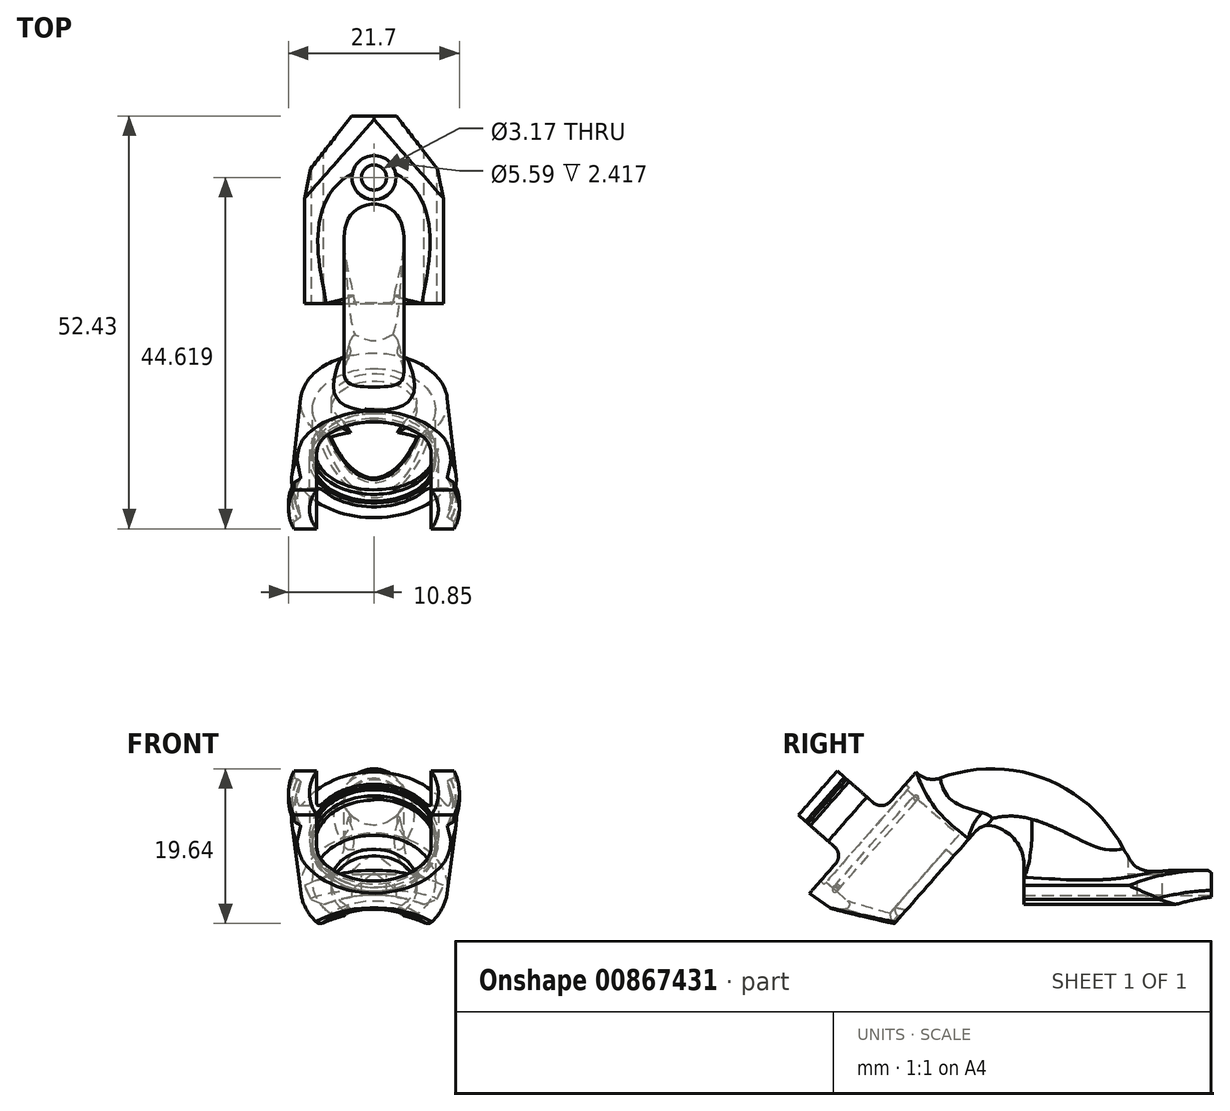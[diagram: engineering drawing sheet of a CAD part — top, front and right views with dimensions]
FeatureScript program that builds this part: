
annotation { "Feature Type Name" : "Feature", "Feature Type Description" : "" }
export const myFeature = defineFeature(function(context is Context, id is Id, definition is map)
    precondition{}
    {
        {
            var Q0;
            Q0=qCreatedBy(makeId("Front.planeOp"),FACE);
            var sketch = newSketch(context, id + "F0", { "sketchPlane" : qUnion([Q0])});
            skCircle(sketch, "E0", {"center": v(0, 0) * mm, "radius": 17.69 * mm, "construction": true});
            skCircle(sketch, "E1", {"center": v(0, 0) * mm, "radius": 14.13 * mm});
            skSolve(sketch);
        }
        {
            var Q0;
            Q0=qCreatedBy(makeId("Right.planeOp"),FACE);
            var sketch = newSketch(context, id + "F1", { "sketchPlane" : qUnion([Q0])});
            skLineSegment(sketch, "E2.0", {"start": v(0, -17.69) * mm, "end": v(0, 17.69) * mm, "construction": true});
            skLineSegment(sketch, "E3", {"start": v(0, 17.69) * mm, "end": v(-11.11, 17.69) * mm, "construction": true});
            skLineSegment(sketch, "E4", {"start": v(0, 17.69) * mm, "end": v(12.7, 17.69) * mm});
            skLineSegment(sketch, "E5", {"start": v(0, 17.69) * mm, "end": v(-11.11, 17.69) * mm});
            skLineSegment(sketch, "E6", {"start": v(-11.11, 17.69) * mm, "end": v(-11.11, 20.86) * mm});
            skLineSegment(sketch, "E7", {"start": v(-11.11, 20.86) * mm, "end": v(12.7, 20.86) * mm});
            skLineSegment(sketch, "E8", {"start": v(12.7, 20.86) * mm, "end": v(12.7, 17.69) * mm});
            skLineSegment(sketch, "E9", {"start": v(0, 0) * mm, "end": v(-2.54, 0) * mm, "construction": true});
            skLineSegment(sketch, "E10", {"start": v(-11.11, 17.69) * mm, "end": v(-22.65, 17.69) * mm, "construction": true});
            skLineSegment(sketch, "E11", {"start": v(-2.54, 0) * mm, "end": v(-22.65, 17.69) * mm});
            skLineSegment(sketch, "E12", {"start": v(-2.54, 0) * mm, "end": v(2.5, 5.72) * mm});
            skLineSegment(sketch, "E13", {"start": v(2.5, 5.72) * mm, "end": v(-11.11, 17.69) * mm});
            skLineSegment(sketch, "E14", {"start": v(-2.54, 0) * mm, "end": v(-7.57, -5.72) * mm});
            skLineSegment(sketch, "E15", {"start": v(-7.57, -5.72) * mm, "end": v(-34.2, 17.69) * mm});
            skLineSegment(sketch, "E16", {"start": v(-29.66, 13.58) * mm, "end": v(-24.51, 19.44) * mm, "construction": true});
            skLineSegment(sketch, "E17", {"start": v(-19.36, 25.3) * mm, "end": v(-25.92, 31.06) * mm});
            skLineSegment(sketch, "E18", {"start": v(-19.36, 25.3) * mm, "end": v(-20.93, 23.5) * mm});
            skLineSegment(sketch, "E19", {"start": v(-20.93, 23.5) * mm, "end": v(-19.98, 22.67) * mm});
            skLineSegment(sketch, "E20", {"start": v(-19.98, 22.67) * mm, "end": v(-17.4, 25.6) * mm});
            skLineSegment(sketch, "E21", {"start": v(-17.4, 25.6) * mm, "end": v(-24.91, 32.2) * mm});
            skLineSegment(sketch, "E22", {"start": v(-25.92, 31.06) * mm, "end": v(-24.91, 32.2) * mm});
            skLineSegment(sketch, "E23", {"start": v(-25.67, 31.35) * mm, "end": v(-31.87, 36.8) * mm});
            skLineSegment(sketch, "E24", {"start": v(-31.87, 36.8) * mm, "end": v(-31.11, 37.66) * mm});
            skLineSegment(sketch, "E25", {"start": v(-24.91, 32.2) * mm, "end": v(-31.11, 37.66) * mm});
            skLineSegment(sketch, "E26", {"start": v(-31.11, 37.66) * mm, "end": v(-30.1, 38.8) * mm});
            skLineSegment(sketch, "E27", {"start": v(-30.1, 38.8) * mm, "end": v(-28.91, 37.75) * mm});
            skLineSegment(sketch, "E28", {"start": v(-28.91, 37.75) * mm, "end": v(-29.92, 36.6) * mm});
            skLineSegment(sketch, "E29", {"start": v(-24.51, 19.44) * mm, "end": v(-29.7, 24) * mm, "construction": true});
            skCircle(sketch, "E30", {"center": v(-24.81, 30.09) * mm, "radius": 0.33 * mm});
            skLineSegment(sketch, "E31", {"start": v(-27.34, 34.34) * mm, "end": v(-26.59, 35.2) * mm});
            skLineSegment(sketch, "E32", {"start": v(-26.59, 35.2) * mm, "end": v(-17.4, 25.6) * mm});
            skLineSegment(sketch, "E33", {"start": v(-22.65, 17.69) * mm, "end": v(-34.2, 17.69) * mm, "construction": true});
            skPoint(sketch, "E34", {"position": v(-28.42, 17.69) * mm});
            skLineSegment(sketch, "E35", {"start": v(-24.51, 19.44) * mm, "end": v(-19.36, 25.3) * mm, "construction": true});
            skPoint(sketch, "E36", {"position": v(-27.09, 16.51) * mm});
            skLineSegment(sketch, "E37", {"start": v(-26.59, 35.2) * mm, "end": v(-29.5, 37.09) * mm});
            skSolve(sketch);
        }
        {
            var Q0;
            Q0=makeQuery(id+"F1.imprint","IMPRINT",FACE,{"disambiguationData":[TD([[makeQuery(id+"F1.imprint","IMPRINT",EDGE,{"derivedFrom":sQuery(id+"F1.wireOp",EDGE,"E4")}),1.0]])]});
            var Q1;
            Q1=sQuery(id+"F1.wireOp",EDGE,"E9");
            revolve(context, id + "F2", {"surfaceOperationType" : NewSurfaceOperationType.NEW, "entities" : qUnion([Q0]), "axis" : qUnion([Q1]), "revolveType" : RevolveType.SYMMETRIC, "angle" : 50 * degree});
        }
        {
            var Q0;
            {var subQ0=sQuery(id+"F1.wireOp",EDGE,"E17");Q0=makeQuery(id+"F1.imprint","IMPRINT",FACE,{"disambiguationData":[TD([[makeQuery(id+"F1.imprint","IMPRINT",EDGE,{"derivedFrom":subQ0}),-1.0]])]});}
            var Q1;
            {var subQ5=sQuery(id+"F1.wireOp",EDGE,"E23");Q1=makeQuery(id+"F1.imprint","IMPRINT",FACE,{"disambiguationData":[TD([[makeQuery(id+"F1.imprint","IMPRINT",EDGE,{"derivedFrom":subQ5}),-1.0]])]});}
            var Q2;
            {var subQ0=sQuery(id+"F1.wireOp",EDGE,"E26");Q2=makeQuery(id+"F1.imprint","IMPRINT",FACE,{"disambiguationData":[TD([[makeQuery(id+"F1.imprint","IMPRINT",EDGE,{"derivedFrom":subQ0}),-1.0]])]});}
            var Q3;
            {var subQ0=sQuery(id+"F1.wireOp",EDGE,"E21");Q3=makeQuery(id+"F1.imprint","IMPRINT",FACE,{"disambiguationData":[TD([[makeQuery(id+"F1.imprint","IMPRINT",EDGE,{"derivedFrom":subQ0}),-1.0]])]});}
            var Q4;
            {var subQ0=sQuery(id+"F1.wireOp",EDGE,"E30");var subQ1=sQuery(id+"F1.wireOp",EDGE,"E17");var subQ2=makeQuery(id+"F1.imprint","INTERSECT",VERTEX,{"disambiguationData":[OD(0.0)],"derivedFrom":[subQ1,subQ0]});Q4=makeQuery(id+"F1.imprint","IMPRINT",FACE,{"disambiguationData":[TD([[makeQuery(id+"F1.imprint","IMPRINT",EDGE,{"disambiguationData":[TD([[subQ2,-1.0]])],"derivedFrom":subQ1}),-1.0]])]});}
            var Q5;
            {var subQ5=sQuery(id+"F1.wireOp",EDGE,"1z6JYlKL-7tiU-9kOK-F6vj-neqsAa9XEWl2");Q5=makeQuery(id+"F1.imprint","IMPRINT",FACE,{"disambiguationData":[TD([[makeQuery(id+"F1.imprint","IMPRINT",EDGE,{"derivedFrom":subQ5}),1.0]])]});}
            var Q6;
            {var subQ3=sQuery(id+"F1.wireOp",EDGE,"E31");Q6=makeQuery(id+"F1.imprint","IMPRINT",FACE,{"disambiguationData":[TD([[makeQuery(id+"F1.imprint","IMPRINT",EDGE,{"derivedFrom":subQ3}),1.0]])]});}
            var Q7;
            Q7=sQuery(id+"F1.wireOp",EDGE,"E29");
            revolve(context, id + "F3", {"surfaceOperationType" : NewSurfaceOperationType.NEW, "entities" : qUnion([Q0, Q1, Q2, Q3, Q4, Q5, Q6]), "axis" : qUnion([Q7]), "revolveType" : RevolveType.FULL});
        }
        {
            var Q0;
            Q0=qCreatedBy(makeId("Top.planeOp"),FACE);
            cPlane(context, id + "F4", {"entities" : qUnion([Q0]), "cplaneType" : CPlaneType.OFFSET, "offset" : 20.32 * mm, "width" : 152.4 * mm, "height" : 152.4 * mm});
        }
        {
            var Q0;
            Q0=qCreatedBy(id+"F4.planeOp",FACE);
            var sketch = newSketch(context, id + "F5", { "sketchPlane" : qUnion([Q0])});
            skPoint(sketch, "E38.0", {"position": v(0, -11.11) * mm});
            skCircle(sketch, "E39", {"center": v(0, 4.89) * mm, "radius": 1.59 * mm});
            skSolve(sketch);
        }
        {
            var Q0;
            Q0=makeQuery(id+"F5.imprint","IMPRINT",FACE,{"disambiguationData":[TD([[makeQuery(id+"F5.imprint","IMPRINT",EDGE,{"derivedFrom":sQuery(id+"F5.wireOp",EDGE,"E39")}),1.0]])]});
            extrude(context, id + "F6", {"entities" : qUnion([Q0]), "operationType" : NewBodyOperationType.REMOVE, "endBound" : BoundingType.SYMMETRIC, "oppositeDirection" : true, "depth" : 25.4 * mm, "offsetDistance" : 25.4 * mm});
        }
        {
            var Q0;
            Q0=qCreatedBy(id+"F4.planeOp",FACE);
            var sketch = newSketch(context, id + "F7", { "sketchPlane" : qUnion([Q0])});
            skCircle(sketch, "E40", {"center": v(0, -0.95) * mm, "radius": 3.81 * mm});
            skPoint(sketch, "E41.0", {"position": v(0, -11.11) * mm});
            skSolve(sketch);
        }
        {
            var Q0;
            Q0=qCreatedBy(makeId("Right.planeOp"),FACE);
            var sketch = newSketch(context, id + "F8", { "sketchPlane" : qUnion([Q0])});
            skPoint(sketch, "E42.0", {"position": v(-11.11, 20.32) * mm});
            skLineSegment(sketch, "E42.1", {"start": v(3.3, 20.32) * mm, "end": v(6.48, 20.32) * mm, "construction": true});
            skLineSegment(sketch, "E43.0", {"start": v(-25.92, 31.06) * mm, "end": v(-36.22, 19.35) * mm, "construction": true});
            skLineSegment(sketch, "E43.1", {"start": v(-19.36, 25.3) * mm, "end": v(-29.66, 13.58) * mm, "construction": true});
            skLineSegment(sketch, "E44", {"start": v(-19.36, 25.3) * mm, "end": v(-25.92, 31.06) * mm, "construction": true});
            skArc(sketch, "E45", {"start": v(-0.95, 20.32) * mm, "mid": v(-10, 29.21) * mm, "end": v(-22.64, 28.18) * mm});
            skLineSegment(sketch, "E46.0", {"start": v(-4.76, 20.32) * mm, "end": v(2.86, 20.32) * mm});
            skPoint(sketch, "E47", {"position": v(-0.95, 20.32) * mm});
            skArc(sketch, "E48", {"start": v(-0.95, 20.32) * mm, "mid": v(-10.69, 29.44) * mm, "end": v(-23.88, 27.4) * mm});
            skLineSegment(sketch, "E49", {"start": v(-20.28, 24.25) * mm, "end": v(-26.84, 30.01) * mm});
            skSolve(sketch);
        }
        {
            var Q0;
            Q0 = qSketchRegion(id + "F7", true);
            var Q1;
            Q1=sQuery(id+"F8.wireOp",EDGE,"E48");
            sweep(context, id + "F9", {"operationType" : NewBodyOperationType.ADD, "profiles" : qUnion([Q0]), "path" : qUnion([Q1])});
        }
        {
            var Q0;
            Q0=makeQuery(id+"F2.opRevolve","CAP_EDGE",EDGE,{"disambiguationData":[OSD([sQuery(id+"F1.wireOp",EDGE,"E4"),sQuery(id+"F1.wireOp",EDGE,"E5")])],"isStart":true});
            var Q1;
            Q1=makeQuery(id+"F2.opRevolve","CAP_EDGE",EDGE,{"disambiguationData":[OSD([sQuery(id+"F1.wireOp",EDGE,"E4"),sQuery(id+"F1.wireOp",EDGE,"E5")])],"isStart":false});
            chamfer(context, id + "F10", {"entities" : qUnion([Q0, Q1]), "width" : 1.27 * mm, "tangentPropagation" : true});
        }
        {
            var Q0;
            Q0=makeQuery(id+"F0.imprint","IMPRINT",FACE,{"disambiguationData":[TD([[makeQuery(id+"F0.imprint","IMPRINT",EDGE,{"derivedFrom":sQuery(id+"F0.wireOp",EDGE,"E1")}),1.0]])]});
            extrude(context, id + "F11", {"entities" : qUnion([Q0]), "operationType" : NewBodyOperationType.REMOVE, "depth" : 43.43 * mm, "offsetDistance" : 25.4 * mm, "hasDraft" : true, "draftAngle" : 3 * degree});
        }
        {
            var Q0;
            Q0=qCreatedBy(id+"F4.planeOp",FACE);
            var sketch = newSketch(context, id + "F12", { "sketchPlane" : qUnion([Q0])});
            skCircle(sketch, "E50.0", {"center": v(0, 4.89) * mm, "radius": 1.59 * mm});
            skCircle(sketch, "E51", {"center": v(0, 4.89) * mm, "radius": 2.8 * mm});
            skSolve(sketch);
        }
        {
            var Q0;
            Q0=makeQuery(id+"F3.opRevolve","SWEPT_EDGE",EDGE,{"disambiguationData":[OSD([sQuery(id+"F1.wireOp",EDGE,"E25"),sQuery(id+"F1.wireOp",EDGE,"E28")])]});
            chamfer(context, id + "F13", {"entities" : qUnion([Q0]), "width" : 0.38 * mm, "tangentPropagation" : true});
        }
        {
            var Q0;
            Q0=makeQuery(id+"F3.opRevolve","SWEPT_FACE",FACE,{"disambiguationData":[OSD([sQuery(id+"F1.wireOp",EDGE,"E22")])]});
            var sketch = newSketch(context, id + "F14", { "sketchPlane" : qUnion([Q0])});
            skCircle(sketch, "E52.0", {"center": v(0, -1.59) * mm, "radius": 7.8 * mm});
            skSolve(sketch);
        }
        {
            var Q0;
            Q0=makeQuery(id+"F14.imprint","IMPRINT",FACE,{"disambiguationData":[TD([[makeQuery(id+"F14.imprint","IMPRINT",EDGE,{"derivedFrom":sQuery(id+"F14.wireOp",EDGE,"E52.0")}),-1.0]])]});
            extrude(context, id + "F15", {"entities" : qUnion([Q0]), "operationType" : NewBodyOperationType.REMOVE, "oppositeDirection" : true, "depth" : 8.73 * mm, "offsetDistance" : 25.4 * mm});
        }
        {
            var Q0;
            {var subQ0=sQuery(id+"F1.wireOp",EDGE,"E17");Q0=makeQuery(id+"F1.imprint","IMPRINT",FACE,{"disambiguationData":[TD([[makeQuery(id+"F1.imprint","IMPRINT",EDGE,{"derivedFrom":subQ0}),1.0]])]});}
            var Q1;
            Q1=sQuery(id+"F1.wireOp",EDGE,"E29");
            revolve(context, id + "F16", {"operationType" : NewBodyOperationType.ADD, "surfaceOperationType" : NewSurfaceOperationType.NEW, "entities" : qUnion([Q0]), "axis" : qUnion([Q1]), "revolveType" : RevolveType.ONE_DIRECTION, "angle" : 200 * degree});
        }
        {
            var Q0;
            Q0=makeQuery(id+"F9.boolean.opBoolean","INTERSECT",EDGE,{"derivedFrom":[makeQuery(id+"F2.opRevolve","SWEPT_FACE",FACE,{"disambiguationData":[OSD([sQuery(id+"F1.wireOp",EDGE,"E7")])]}),makeQuery(id+"F9.opSweep","SWEPT_FACE",FACE,{"disambiguationData":[OSD([sQuery(id+"F7.wireOp",EDGE,"E40"),sQuery(id+"F8.wireOp",EDGE,"E48")])]})]});
            fillet(context, id + "F17", {"entities" : qUnion([Q0]), "radius" : 5.08 * mm, "tangentPropagation" : true, "allowEdgeOverflow" : false});
        }
        {
            var Q0;
            Q0 = qSketchRegion(id + "F12", true);
            extrude(context, id + "F18", {"entities" : qUnion([Q0]), "operationType" : NewBodyOperationType.REMOVE, "depth" : 25.4 * mm, "offsetDistance" : 25.4 * mm});
        }
        {
            var Q0;
            Q0=makeQuery(id+"F3.opRevolve","SWEPT_FACE",FACE,{"disambiguationData":[OSD([sQuery(id+"F1.wireOp",EDGE,"E24"),sQuery(id+"F1.wireOp",EDGE,"E26")])]});
            var sketch = newSketch(context, id + "F19", { "sketchPlane" : qUnion([Q0])});
            skCircle(sketch, "E53.0", {"center": v(0, -1.59) * mm, "radius": 8.18 * mm});
            skLineSegment(sketch, "E54.bottom", {"start": v(12.7, 11.04) * mm, "end": v(-12.7, 11.04) * mm});
            skLineSegment(sketch, "E54.top", {"start": v(12.7, 2.15) * mm, "end": v(-12.7, 2.15) * mm});
            skLineSegment(sketch, "E54.left", {"start": v(12.7, 11.04) * mm, "end": v(12.7, 2.15) * mm});
            skLineSegment(sketch, "E54.right", {"start": v(-12.7, 11.04) * mm, "end": v(-12.7, 2.15) * mm});
            skPoint(sketch, "E54.middle", {"position": v(0, 6.6) * mm});
            skLineSegment(sketch, "E55.bottom", {"start": v(12.7, -14.21) * mm, "end": v(-12.7, -14.21) * mm});
            skLineSegment(sketch, "E55.top", {"start": v(12.7, -5.32) * mm, "end": v(-12.7, -5.32) * mm});
            skLineSegment(sketch, "E55.left", {"start": v(12.7, -14.21) * mm, "end": v(12.7, -5.32) * mm});
            skLineSegment(sketch, "E55.right", {"start": v(-12.7, -14.21) * mm, "end": v(-12.7, -5.32) * mm});
            skPoint(sketch, "E55.middle", {"position": v(0, -9.77) * mm});
            skSolve(sketch);
        }
        {
            var Q0;
            Q0 = qSketchRegion(id + "F19", true);
            extrude(context, id + "F20", {"entities" : qUnion([Q0]), "operationType" : NewBodyOperationType.REMOVE, "oppositeDirection" : true, "depth" : 7.62 * mm, "offsetDistance" : 25.4 * mm});
        }
        {
            var Q0;
            {var subQ0=sQuery(id+"F19.wireOp",EDGE,"E54.top");Q0=makeQuery(id+"F20.boolean.opBoolean","COPY",EDGE,{"derivedFrom":makeQuery(id+"F20.opExtrude","CAP_EDGE",EDGE,{"disambiguationData":[OSD([subQ0]),TDD([makeQuery(id+"F19.imprint","IMPRINT",EDGE,{"disambiguationData":[TD([[makeQuery(id+"F19.imprint","INTERSECT",VERTEX,{"disambiguationData":[OD(1.0)],"derivedFrom":[sQuery(id+"F19.wireOp",EDGE,"E53.0"),subQ0]}),-1.0]])],"derivedFrom":subQ0}),makeQuery(id+"F19.imprint","IMPRINT",EDGE,{"disambiguationData":[TD([[makeQuery(id+"F19.imprint","INTERSECT",VERTEX,{"derivedFrom":[subQ0,sQuery(id+"F19.wireOp",EDGE,"E54.right")]}),1.0]])],"derivedFrom":subQ0})])],"isStart":false})});}
            var Q1;
            {var subQ0=sQuery(id+"F19.wireOp",EDGE,"E54.top");Q1=makeQuery(id+"F20.boolean.opBoolean","COPY",EDGE,{"derivedFrom":makeQuery(id+"F20.opExtrude","CAP_EDGE",EDGE,{"disambiguationData":[OSD([subQ0]),TDD([makeQuery(id+"F19.imprint","IMPRINT",EDGE,{"disambiguationData":[TD([[makeQuery(id+"F19.imprint","INTERSECT",VERTEX,{"derivedFrom":[subQ0,sQuery(id+"F19.wireOp",EDGE,"E54.left")]}),-1.0]])],"derivedFrom":subQ0}),makeQuery(id+"F19.imprint","IMPRINT",EDGE,{"disambiguationData":[TD([[makeQuery(id+"F19.imprint","INTERSECT",VERTEX,{"disambiguationData":[OD(0.0)],"derivedFrom":[sQuery(id+"F19.wireOp",EDGE,"E53.0"),subQ0]}),1.0]])],"derivedFrom":subQ0})])],"isStart":false})});}
            var Q2;
            {var subQ0=sQuery(id+"F19.wireOp",EDGE,"E55.top");Q2=makeQuery(id+"F20.boolean.opBoolean","COPY",EDGE,{"derivedFrom":makeQuery(id+"F20.opExtrude","CAP_EDGE",EDGE,{"disambiguationData":[OSD([subQ0]),TDD([makeQuery(id+"F19.imprint","IMPRINT",EDGE,{"disambiguationData":[TD([[makeQuery(id+"F19.imprint","INTERSECT",VERTEX,{"disambiguationData":[OD(1.0)],"derivedFrom":[sQuery(id+"F19.wireOp",EDGE,"E53.0"),subQ0]}),-1.0]])],"derivedFrom":subQ0}),makeQuery(id+"F19.imprint","IMPRINT",EDGE,{"disambiguationData":[TD([[makeQuery(id+"F19.imprint","INTERSECT",VERTEX,{"derivedFrom":[subQ0,sQuery(id+"F19.wireOp",EDGE,"E55.right")]}),1.0]])],"derivedFrom":subQ0})])],"isStart":false})});}
            var Q3;
            {var subQ0=sQuery(id+"F19.wireOp",EDGE,"E55.top");Q3=makeQuery(id+"F20.boolean.opBoolean","COPY",EDGE,{"derivedFrom":makeQuery(id+"F20.opExtrude","CAP_EDGE",EDGE,{"disambiguationData":[OSD([subQ0]),TDD([makeQuery(id+"F19.imprint","IMPRINT",EDGE,{"disambiguationData":[TD([[makeQuery(id+"F19.imprint","INTERSECT",VERTEX,{"derivedFrom":[subQ0,sQuery(id+"F19.wireOp",EDGE,"E55.left")]}),-1.0]])],"derivedFrom":subQ0}),makeQuery(id+"F19.imprint","IMPRINT",EDGE,{"disambiguationData":[TD([[makeQuery(id+"F19.imprint","INTERSECT",VERTEX,{"disambiguationData":[OD(0.0)],"derivedFrom":[sQuery(id+"F19.wireOp",EDGE,"E53.0"),subQ0]}),1.0]])],"derivedFrom":subQ0})])],"isStart":false})});}
            fillet(context, id + "F21", {"entities" : qUnion([Q0, Q1, Q2, Q3]), "radius" : 1.52 * mm, "tangentPropagation" : true, "allowEdgeOverflow" : false});
        }
        {
            var Q0;
            Q0=qCreatedBy(makeId("Top.planeOp"),FACE);
            var sketch = newSketch(context, id + "F22", { "sketchPlane" : qUnion([Q0])});
            skLineSegment(sketch, "E56", {"start": v(0, 0) * mm, "end": v(12.7, 0) * mm});
            skLineSegment(sketch, "E57", {"start": v(0, 0) * mm, "end": v(-12.7, 0) * mm});
            skLineSegment(sketch, "E58", {"start": v(-12.7, 0) * mm, "end": v(0, 16.38) * mm});
            skLineSegment(sketch, "E59", {"start": v(0, 16.38) * mm, "end": v(12.7, 0) * mm});
            skLineSegment(sketch, "E60", {"start": v(-12.7, 0) * mm, "end": v(-12.7, 23.27) * mm});
            skLineSegment(sketch, "E61", {"start": v(-12.7, 23.27) * mm, "end": v(12.7, 23.27) * mm});
            skLineSegment(sketch, "E62", {"start": v(12.7, 23.27) * mm, "end": v(12.7, 0) * mm});
            skSolve(sketch);
        }
        {
            var Q0;
            Q0=makeQuery(id+"F22.imprint","IMPRINT",FACE,{"disambiguationData":[TD([[makeQuery(id+"F22.imprint","IMPRINT",EDGE,{"derivedFrom":sQuery(id+"F22.wireOp",EDGE,"E58")}),1.0]])]});
            extrude(context, id + "F23", {"entities" : qUnion([Q0]), "operationType" : NewBodyOperationType.REMOVE, "depth" : 25.4 * mm, "offsetDistance" : 25.4 * mm});
        }
        {
            var Q0;
            Q0=makeQuery(id+"F23.boolean.opBoolean","INTERSECT",EDGE,{"derivedFrom":[makeQuery(id+"F2.opRevolve","SWEPT_FACE",FACE,{"disambiguationData":[OSD([sQuery(id+"F1.wireOp",EDGE,"E7")])]}),makeQuery(id+"F23.opExtrude","SWEPT_FACE",FACE,{"disambiguationData":[OSD([sQuery(id+"F22.wireOp",EDGE,"E58")])]})]});
            var Q1;
            Q1=makeQuery(id+"F23.boolean.opBoolean","INTERSECT",EDGE,{"derivedFrom":[makeQuery(id+"F2.opRevolve","SWEPT_FACE",FACE,{"disambiguationData":[OSD([sQuery(id+"F1.wireOp",EDGE,"E7")])]}),makeQuery(id+"F23.opExtrude","SWEPT_FACE",FACE,{"disambiguationData":[OSD([sQuery(id+"F22.wireOp",EDGE,"E59")])]})]});
            chamfer(context, id + "F24", {"entities" : qUnion([Q0, Q1]), "width" : 2.54 * mm, "tangentPropagation" : true});
        }
        {
            var Q0;
            Q0=makeQuery(id+"F11.boolean.opBoolean","COPY",FACE,{"derivedFrom":makeQuery(id+"F11.opExtrude","SWEPT_FACE",FACE,{"disambiguationData":[OSD([sQuery(id+"F0.wireOp",EDGE,"E1")])]})});
            fillet(context, id + "F25", {"entities" : qUnion([Q0]), "radius" : 0.58 * mm, "tangentPropagation" : true, "allowEdgeOverflow" : false});
        }
        {
            var Q0;
            Q0=makeQuery(id+"F9.boolean.opBoolean","INTERSECT",EDGE,{"derivedFrom":[makeQuery(id+"F3.opRevolve","SWEPT_FACE",FACE,{"disambiguationData":[OSD([sQuery(id+"F1.wireOp",EDGE,"E32")])]}),makeQuery(id+"F9.opSweep","SWEPT_FACE",FACE,{"disambiguationData":[OSD([sQuery(id+"F7.wireOp",EDGE,"E40"),sQuery(id+"F8.wireOp",EDGE,"E48")])]})]});
            fillet(context, id + "F26", {"entities" : qUnion([Q0]), "radius" : 2.82 * mm, "tangentPropagation" : true, "allowEdgeOverflow" : false});
        }
    });
